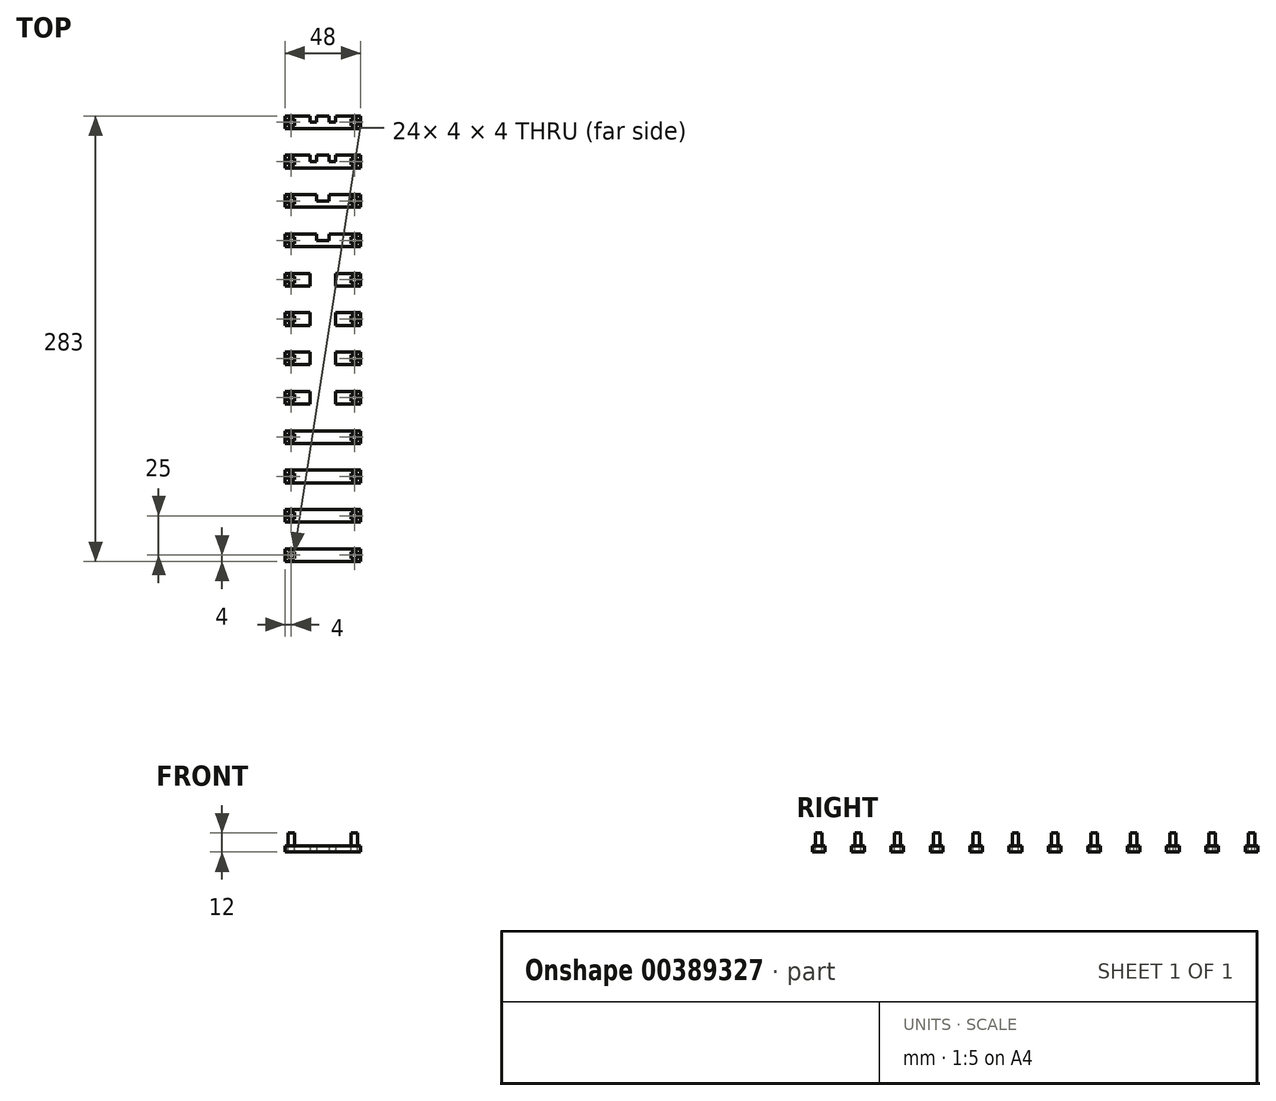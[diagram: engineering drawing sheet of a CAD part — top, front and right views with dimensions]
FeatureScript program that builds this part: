
annotation { "Feature Type Name" : "Feature", "Feature Type Description" : "" }
export const myFeature = defineFeature(function(context is Context, id is Id, definition is map)
    precondition{}
    {
        {
            assignVariable(context, id + "F0", {"name" : "WT", "anyValue" : 4});
        }
        {
            var Q0;
            Q0=qCreatedBy(makeId("Top.planeOp"),FACE);
            var sketch = newSketch(context, id + "F1", { "sketchPlane" : qUnion([Q0])});
            skLineSegment(sketch, "E0.bottom", {"start": v(-24, 4) * mm, "end": v(24, 4) * mm});
            skLineSegment(sketch, "E0.top", {"start": v(-24, -4) * mm, "end": v(24, -4) * mm});
            skLineSegment(sketch, "E0.left", {"start": v(-24, 4) * mm, "end": v(-24, -4) * mm});
            skLineSegment(sketch, "E0.right", {"start": v(24, 4) * mm, "end": v(24, -4) * mm});
            skPoint(sketch, "E0.middle", {"position": v(0, 0) * mm});
            skLineSegment(sketch, "E1.0.1.0", {"start": v(-24, 21) * mm, "end": v(24, 21) * mm});
            skLineSegment(sketch, "E1.0.1.1", {"start": v(-24, 29) * mm, "end": v(-24, 21) * mm});
            skLineSegment(sketch, "E1.0.1.2", {"start": v(-24, 29) * mm, "end": v(24, 29) * mm});
            skLineSegment(sketch, "E1.0.1.3", {"start": v(24, 29) * mm, "end": v(24, 21) * mm});
            skLineSegment(sketch, "E1.0.2.0", {"start": v(-24, 46) * mm, "end": v(24, 46) * mm});
            skLineSegment(sketch, "E1.0.2.1", {"start": v(-24, 54) * mm, "end": v(-24, 46) * mm});
            skLineSegment(sketch, "E1.0.2.2", {"start": v(-24, 54) * mm, "end": v(24, 54) * mm});
            skLineSegment(sketch, "E1.0.2.3", {"start": v(24, 54) * mm, "end": v(24, 46) * mm});
            skLineSegment(sketch, "E1.0.3.0", {"start": v(-24, 71) * mm, "end": v(24, 71) * mm});
            skLineSegment(sketch, "E1.0.3.1", {"start": v(-24, 79) * mm, "end": v(-24, 71) * mm});
            skLineSegment(sketch, "E1.0.3.2", {"start": v(-24, 79) * mm, "end": v(24, 79) * mm});
            skLineSegment(sketch, "E1.0.3.3", {"start": v(24, 79) * mm, "end": v(24, 71) * mm});
            skLineSegment(sketch, "E1.direction1", {"start": v(-35, -4) * mm, "end": v(-24, -4) * mm, "construction": true});
            skLineSegment(sketch, "E1.direction2", {"start": v(-24, -4) * mm, "end": v(-24, 21) * mm, "construction": true});
            skLineSegment(sketch, "E2.0.0.4", {"start": v(-24, 96) * mm, "end": v(24, 96) * mm});
            skLineSegment(sketch, "E2.3.0.4", {"start": v(-24, 104) * mm, "end": v(-24, 96) * mm});
            skLineSegment(sketch, "E2.6.0.4", {"start": v(-24, 104) * mm, "end": v(24, 104) * mm});
            skLineSegment(sketch, "E2.9.0.4", {"start": v(24, 104) * mm, "end": v(24, 96) * mm});
            skLineSegment(sketch, "E2.0.0.5", {"start": v(-24, 121) * mm, "end": v(24, 121) * mm});
            skLineSegment(sketch, "E2.3.0.5", {"start": v(-24, 129) * mm, "end": v(-24, 121) * mm});
            skLineSegment(sketch, "E2.6.0.5", {"start": v(-24, 129) * mm, "end": v(24, 129) * mm});
            skLineSegment(sketch, "E2.9.0.5", {"start": v(24, 129) * mm, "end": v(24, 121) * mm});
            skLineSegment(sketch, "E2.0.0.6", {"start": v(-24, 146) * mm, "end": v(24, 146) * mm});
            skLineSegment(sketch, "E2.3.0.6", {"start": v(-24, 154) * mm, "end": v(-24, 146) * mm});
            skLineSegment(sketch, "E2.6.0.6", {"start": v(-24, 154) * mm, "end": v(24, 154) * mm});
            skLineSegment(sketch, "E2.9.0.6", {"start": v(24, 154) * mm, "end": v(24, 146) * mm});
            skLineSegment(sketch, "E2.0.0.7", {"start": v(-24, 171) * mm, "end": v(24, 171) * mm});
            skLineSegment(sketch, "E2.3.0.7", {"start": v(-24, 179) * mm, "end": v(-24, 171) * mm});
            skLineSegment(sketch, "E2.6.0.7", {"start": v(-24, 179) * mm, "end": v(24, 179) * mm});
            skLineSegment(sketch, "E2.9.0.7", {"start": v(24, 179) * mm, "end": v(24, 171) * mm});
            skLineSegment(sketch, "E3", {"start": v(-8, 96) * mm, "end": v(-8, 179) * mm});
            skLineSegment(sketch, "E4", {"start": v(8, 179) * mm, "end": v(8, 96) * mm});
            skLineSegment(sketch, "E5.0.0.8", {"start": v(-24, 196) * mm, "end": v(24, 196) * mm});
            skLineSegment(sketch, "E5.3.0.8", {"start": v(-24, 204) * mm, "end": v(-24, 196) * mm});
            skLineSegment(sketch, "E5.6.0.8", {"start": v(-24, 204) * mm, "end": v(24, 204) * mm});
            skLineSegment(sketch, "E5.9.0.8", {"start": v(24, 204) * mm, "end": v(24, 196) * mm});
            skLineSegment(sketch, "E5.0.0.9", {"start": v(-24, 221) * mm, "end": v(24, 221) * mm});
            skLineSegment(sketch, "E5.3.0.9", {"start": v(-24, 229) * mm, "end": v(-24, 221) * mm});
            skLineSegment(sketch, "E5.6.0.9", {"start": v(-24, 229) * mm, "end": v(24, 229) * mm});
            skLineSegment(sketch, "E5.9.0.9", {"start": v(24, 229) * mm, "end": v(24, 221) * mm});
            skLineSegment(sketch, "E5.0.0.10", {"start": v(-24, 246) * mm, "end": v(24, 246) * mm});
            skLineSegment(sketch, "E5.3.0.10", {"start": v(-24, 254) * mm, "end": v(-24, 246) * mm});
            skLineSegment(sketch, "E5.6.0.10", {"start": v(-24, 254) * mm, "end": v(24, 254) * mm});
            skLineSegment(sketch, "E5.9.0.10", {"start": v(24, 254) * mm, "end": v(24, 246) * mm});
            skLineSegment(sketch, "E5.0.0.11", {"start": v(-24, 271) * mm, "end": v(24, 271) * mm});
            skLineSegment(sketch, "E5.3.0.11", {"start": v(-24, 279) * mm, "end": v(-24, 271) * mm});
            skLineSegment(sketch, "E5.6.0.11", {"start": v(-24, 279) * mm, "end": v(24, 279) * mm});
            skLineSegment(sketch, "E5.9.0.11", {"start": v(24, 279) * mm, "end": v(24, 271) * mm});
            skLineSegment(sketch, "E6", {"start": v(-4, 204) * mm, "end": v(-4, 200) * mm});
            skPoint(sketch, "E6.endSnap0", {"position": v(-24, 200) * mm});
            skLineSegment(sketch, "E7", {"start": v(-4, 200) * mm, "end": v(4, 200) * mm});
            skLineSegment(sketch, "E8", {"start": v(4, 200) * mm, "end": v(4, 204) * mm});
            skLineSegment(sketch, "E9", {"start": v(-4, 229) * mm, "end": v(-4, 225) * mm});
            skLineSegment(sketch, "E10", {"start": v(-4, 225) * mm, "end": v(4, 225) * mm});
            skLineSegment(sketch, "E11", {"start": v(4, 225) * mm, "end": v(4, 229) * mm});
            skLineSegment(sketch, "E12", {"start": v(-8, 254) * mm, "end": v(-8, 250) * mm});
            skLineSegment(sketch, "E13", {"start": v(-8, 250) * mm, "end": v(-4, 250) * mm});
            skLineSegment(sketch, "E14", {"start": v(-4, 250) * mm, "end": v(-4, 254) * mm});
            skLineSegment(sketch, "E15", {"start": v(8, 254) * mm, "end": v(8, 250) * mm});
            skLineSegment(sketch, "E16", {"start": v(4, 250) * mm, "end": v(8, 250) * mm});
            skLineSegment(sketch, "E17", {"start": v(4, 250) * mm, "end": v(4, 254) * mm});
            skLineSegment(sketch, "E18", {"start": v(-8, 275) * mm, "end": v(-8, 279) * mm});
            skLineSegment(sketch, "E19", {"start": v(-4, 275) * mm, "end": v(-4, 279) * mm});
            skLineSegment(sketch, "E20", {"start": v(4, 275) * mm, "end": v(4, 279) * mm});
            skLineSegment(sketch, "E21", {"start": v(8, 275) * mm, "end": v(8, 279) * mm});
            skLineSegment(sketch, "E22", {"start": v(-8, 275) * mm, "end": v(-4, 275) * mm});
            skLineSegment(sketch, "E23", {"start": v(4, 275) * mm, "end": v(8, 275) * mm});
            skLineSegment(sketch, "E24", {"start": v(0, 254) * mm, "end": v(0, 271) * mm, "construction": true});
            skLineSegment(sketch, "E25", {"start": v(0, 262.5) * mm, "end": v(-4.81, 262.5) * mm, "construction": true});
            skLineSegment(sketch, "E26", {"start": v(0, 246) * mm, "end": v(0, 229) * mm, "construction": true});
            skLineSegment(sketch, "E27", {"start": v(0, 221) * mm, "end": v(0, 204) * mm, "construction": true});
            skLineSegment(sketch, "E28", {"start": v(0, 237.5) * mm, "end": v(-7.24, 237.5) * mm, "construction": true});
            skLineSegment(sketch, "E29", {"start": v(0, 212.5) * mm, "end": v(-6.88, 212.5) * mm, "construction": true});
            skLineSegment(sketch, "E30", {"start": v(0, 196) * mm, "end": v(0, 179) * mm, "construction": true});
            skLineSegment(sketch, "E31", {"start": v(0, 187.5) * mm, "end": v(4.56, 187.5) * mm, "construction": true});
            skPoint(sketch, "E31.endSnap0", {"position": v(0, 187.5) * mm});
            skLineSegment(sketch, "E32", {"start": v(0, 171) * mm, "end": v(0, 154) * mm, "construction": true});
            skLineSegment(sketch, "E33", {"start": v(0, 162.5) * mm, "end": v(4.36, 162.5) * mm, "construction": true});
            skLineSegment(sketch, "E34", {"start": v(0, 146) * mm, "end": v(0, 129) * mm, "construction": true});
            skLineSegment(sketch, "E35", {"start": v(0, 137.5) * mm, "end": v(2.22, 137.5) * mm, "construction": true});
            skLineSegment(sketch, "E36", {"start": v(0, 121) * mm, "end": v(0, 104) * mm, "construction": true});
            skLineSegment(sketch, "E37", {"start": v(0, 112.5) * mm, "end": v(3.52, 112.5) * mm, "construction": true});
            skLineSegment(sketch, "E38", {"start": v(0, 96) * mm, "end": v(0, 79) * mm, "construction": true});
            skLineSegment(sketch, "E39", {"start": v(0, 87.5) * mm, "end": v(3.87, 87.5) * mm, "construction": true});
            skLineSegment(sketch, "E40", {"start": v(0, 71) * mm, "end": v(0, 54) * mm, "construction": true});
            skLineSegment(sketch, "E41", {"start": v(0, 62.5) * mm, "end": v(4.14, 62.5) * mm, "construction": true});
            skLineSegment(sketch, "E42", {"start": v(0, 46) * mm, "end": v(0, 29) * mm, "construction": true});
            skLineSegment(sketch, "E43", {"start": v(0, 37.5) * mm, "end": v(2.67, 37.5) * mm, "construction": true});
            skLineSegment(sketch, "E44", {"start": v(0, 21) * mm, "end": v(0, 4) * mm, "construction": true});
            skLineSegment(sketch, "E45", {"start": v(0, 12.5) * mm, "end": v(4.27, 12.5) * mm, "construction": true});
            skSolve(sketch);
        }
        {
            var Q0;
            Q0=makeQuery(id+"F1.imprint","IMPRINT",FACE,{"disambiguationData":[TD([[makeQuery(id+"F1.imprint","IMPRINT",EDGE,{"derivedFrom":sQuery(id+"F1.wireOp",EDGE,"E0.bottom")}),-1.0]])]});
            var Q1;
            Q1=makeQuery(id+"F1.imprint","IMPRINT",FACE,{"disambiguationData":[TD([[makeQuery(id+"F1.imprint","IMPRINT",EDGE,{"derivedFrom":sQuery(id+"F1.wireOp",EDGE,"E1.0.1.0")}),1.0]])]});
            var Q2;
            Q2=makeQuery(id+"F1.imprint","IMPRINT",FACE,{"disambiguationData":[TD([[makeQuery(id+"F1.imprint","IMPRINT",EDGE,{"derivedFrom":sQuery(id+"F1.wireOp",EDGE,"E1.0.2.0")}),1.0]])]});
            var Q3;
            Q3=makeQuery(id+"F1.imprint","IMPRINT",FACE,{"disambiguationData":[TD([[makeQuery(id+"F1.imprint","IMPRINT",EDGE,{"derivedFrom":sQuery(id+"F1.wireOp",EDGE,"E1.0.3.0")}),1.0]])]});
            var Q4;
            Q4=makeQuery(id+"F1.imprint","IMPRINT",FACE,{"disambiguationData":[TD([[makeQuery(id+"F1.imprint","IMPRINT",EDGE,{"derivedFrom":sQuery(id+"F1.wireOp",EDGE,"E1.0.4.0")}),1.0]])]});
            var Q5;
            {var subQ0=sQuery(id+"F1.wireOp",EDGE,"E2.3.0.4");Q5=makeQuery(id+"F1.imprint","IMPRINT",FACE,{"disambiguationData":[TD([[makeQuery(id+"F1.imprint","IMPRINT",EDGE,{"derivedFrom":subQ0}),1.0]])]});}
            var Q6;
            {var subQ0=sQuery(id+"F1.wireOp",EDGE,"E2.3.0.5");Q6=makeQuery(id+"F1.imprint","IMPRINT",FACE,{"disambiguationData":[TD([[makeQuery(id+"F1.imprint","IMPRINT",EDGE,{"derivedFrom":subQ0}),1.0]])]});}
            var Q7;
            {var subQ0=sQuery(id+"F1.wireOp",EDGE,"E2.3.0.6");Q7=makeQuery(id+"F1.imprint","IMPRINT",FACE,{"disambiguationData":[TD([[makeQuery(id+"F1.imprint","IMPRINT",EDGE,{"derivedFrom":subQ0}),1.0]])]});}
            var Q8;
            {var subQ0=sQuery(id+"F1.wireOp",EDGE,"E2.3.0.7");Q8=makeQuery(id+"F1.imprint","IMPRINT",FACE,{"disambiguationData":[TD([[makeQuery(id+"F1.imprint","IMPRINT",EDGE,{"derivedFrom":subQ0}),1.0]])]});}
            var Q9;
            {var subQ0=sQuery(id+"F1.wireOp",EDGE,"E2.9.0.7");Q9=makeQuery(id+"F1.imprint","IMPRINT",FACE,{"disambiguationData":[TD([[makeQuery(id+"F1.imprint","IMPRINT",EDGE,{"derivedFrom":subQ0}),-1.0]])]});}
            var Q10;
            {var subQ0=sQuery(id+"F1.wireOp",EDGE,"E2.9.0.6");Q10=makeQuery(id+"F1.imprint","IMPRINT",FACE,{"disambiguationData":[TD([[makeQuery(id+"F1.imprint","IMPRINT",EDGE,{"derivedFrom":subQ0}),-1.0]])]});}
            var Q11;
            {var subQ0=sQuery(id+"F1.wireOp",EDGE,"E2.9.0.5");Q11=makeQuery(id+"F1.imprint","IMPRINT",FACE,{"disambiguationData":[TD([[makeQuery(id+"F1.imprint","IMPRINT",EDGE,{"derivedFrom":subQ0}),-1.0]])]});}
            var Q12;
            {var subQ0=sQuery(id+"F1.wireOp",EDGE,"E2.9.0.4");Q12=makeQuery(id+"F1.imprint","IMPRINT",FACE,{"disambiguationData":[TD([[makeQuery(id+"F1.imprint","IMPRINT",EDGE,{"derivedFrom":subQ0}),-1.0]])]});}
            var Q13;
            Q13=makeQuery(id+"F1.imprint","IMPRINT",FACE,{"disambiguationData":[TD([[makeQuery(id+"F1.imprint","IMPRINT",EDGE,{"derivedFrom":sQuery(id+"F1.wireOp",EDGE,"E5.0.0.8")}),1.0]])]});
            var Q14;
            Q14=makeQuery(id+"F1.imprint","IMPRINT",FACE,{"disambiguationData":[TD([[makeQuery(id+"F1.imprint","IMPRINT",EDGE,{"derivedFrom":sQuery(id+"F1.wireOp",EDGE,"E5.0.0.9")}),1.0]])]});
            var Q15;
            Q15=makeQuery(id+"F1.imprint","IMPRINT",FACE,{"disambiguationData":[TD([[makeQuery(id+"F1.imprint","IMPRINT",EDGE,{"derivedFrom":sQuery(id+"F1.wireOp",EDGE,"E5.0.0.10")}),1.0]])]});
            var Q16;
            Q16=makeQuery(id+"F1.imprint","IMPRINT",FACE,{"disambiguationData":[TD([[makeQuery(id+"F1.imprint","IMPRINT",EDGE,{"derivedFrom":sQuery(id+"F1.wireOp",EDGE,"E5.0.0.11")}),1.0]])]});
            extrude(context, id + "F2", {"entities" : qUnion([Q0, Q1, Q2, Q3, Q4, Q5, Q6, Q7, Q8, Q9, Q10, Q11, Q12, Q13, Q14, Q15, Q16]), "depth" : getVariable(context, 'WT') * mm});
        }
        {
            var Q0;
            Q0=makeQuery(id+"F2.opExtrude","CAP_FACE",FACE,{"disambiguationData":[OSD([sQuery(id+"F1.wireOp",EDGE,"E5.0.0.11"),sQuery(id+"F1.wireOp",EDGE,"E5.3.0.11"),sQuery(id+"F1.wireOp",EDGE,"E5.6.0.11"),sQuery(id+"F1.wireOp",EDGE,"E5.9.0.11"),sQuery(id+"F1.wireOp",EDGE,"E18"),sQuery(id+"F1.wireOp",EDGE,"E19"),sQuery(id+"F1.wireOp",EDGE,"E20"),sQuery(id+"F1.wireOp",EDGE,"E21"),sQuery(id+"F1.wireOp",EDGE,"E22"),sQuery(id+"F1.wireOp",EDGE,"E23")])],"isStart":false});
            var sketch = newSketch(context, id + "F3", { "sketchPlane" : qUnion([Q0])});
            skLineSegment(sketch, "E46", {"start": v(0, 279) * mm, "end": v(0, 302.45) * mm, "construction": true});
            skLineSegment(sketch, "E47.bottom", {"start": v(-22, 277) * mm, "end": v(-18, 277) * mm});
            skLineSegment(sketch, "E47.top", {"start": v(-22, 273) * mm, "end": v(-18, 273) * mm});
            skLineSegment(sketch, "E47.left", {"start": v(-22, 277) * mm, "end": v(-22, 273) * mm});
            skLineSegment(sketch, "E47.right", {"start": v(-18, 277) * mm, "end": v(-18, 273) * mm});
            skPoint(sketch, "E47.middle", {"position": v(-20, 275) * mm});
            skPoint(sketch, "E48", {"position": v(-24, 275) * mm});
            skLineSegment(sketch, "E49.MirrorCS", {"start": v(18, 277) * mm, "end": v(18, 273) * mm});
            skLineSegment(sketch, "E50.MirrorCS", {"start": v(22, 277) * mm, "end": v(18, 277) * mm});
            skLineSegment(sketch, "E51.MirrorCS", {"start": v(22, 277) * mm, "end": v(22, 273) * mm});
            skLineSegment(sketch, "E52.MirrorCS", {"start": v(22, 273) * mm, "end": v(18, 273) * mm});
            skLineSegment(sketch, "E53.MirrorCS", {"start": v(-18, 248) * mm, "end": v(-18, 252) * mm});
            skLineSegment(sketch, "E54.MirrorCS", {"start": v(-22, 252) * mm, "end": v(-18, 252) * mm});
            skLineSegment(sketch, "E55.MirrorCS", {"start": v(-22, 248) * mm, "end": v(-18, 248) * mm});
            skLineSegment(sketch, "E56.MirrorCS", {"start": v(-22, 248) * mm, "end": v(-22, 252) * mm});
            skLineSegment(sketch, "E57.MirrorCS", {"start": v(18, 248) * mm, "end": v(18, 252) * mm});
            skLineSegment(sketch, "E58.MirrorCS", {"start": v(22, 248) * mm, "end": v(18, 248) * mm});
            skLineSegment(sketch, "E59.MirrorCS", {"start": v(22, 248) * mm, "end": v(22, 252) * mm});
            skLineSegment(sketch, "E60.MirrorCS", {"start": v(22, 252) * mm, "end": v(18, 252) * mm});
            skLineSegment(sketch, "E61.MirrorCS", {"start": v(-22, 227) * mm, "end": v(-18, 227) * mm});
            skLineSegment(sketch, "E62.MirrorCS", {"start": v(-18, 227) * mm, "end": v(-18, 223) * mm});
            skLineSegment(sketch, "E63.MirrorCS", {"start": v(-22, 223) * mm, "end": v(-18, 223) * mm});
            skLineSegment(sketch, "E64.MirrorCS", {"start": v(-22, 227) * mm, "end": v(-22, 223) * mm});
            skLineSegment(sketch, "E65.MirrorCS", {"start": v(18, 227) * mm, "end": v(18, 223) * mm});
            skLineSegment(sketch, "E66.MirrorCS", {"start": v(22, 223) * mm, "end": v(18, 223) * mm});
            skLineSegment(sketch, "E67.MirrorCS", {"start": v(22, 227) * mm, "end": v(22, 223) * mm});
            skLineSegment(sketch, "E68.MirrorCS", {"start": v(22, 227) * mm, "end": v(18, 227) * mm});
            skLineSegment(sketch, "E69.MirrorCS", {"start": v(-22, 202) * mm, "end": v(-18, 202) * mm});
            skLineSegment(sketch, "E70.MirrorCS", {"start": v(-18, 198) * mm, "end": v(-18, 202) * mm});
            skLineSegment(sketch, "E71.MirrorCS", {"start": v(-22, 198) * mm, "end": v(-18, 198) * mm});
            skLineSegment(sketch, "E72.MirrorCS", {"start": v(-22, 198) * mm, "end": v(-22, 202) * mm});
            skLineSegment(sketch, "E73.MirrorCS", {"start": v(22, 202) * mm, "end": v(18, 202) * mm});
            skLineSegment(sketch, "E74.MirrorCS", {"start": v(18, 198) * mm, "end": v(18, 202) * mm});
            skLineSegment(sketch, "E75.MirrorCS", {"start": v(22, 198) * mm, "end": v(18, 198) * mm});
            skLineSegment(sketch, "E76.MirrorCS", {"start": v(22, 198) * mm, "end": v(22, 202) * mm});
            skLineSegment(sketch, "E77.MirrorCS", {"start": v(-18, 177) * mm, "end": v(-18, 173) * mm});
            skLineSegment(sketch, "E78.MirrorCS", {"start": v(-22, 173) * mm, "end": v(-18, 173) * mm});
            skLineSegment(sketch, "E79.MirrorCS", {"start": v(-22, 177) * mm, "end": v(-22, 173) * mm});
            skLineSegment(sketch, "E80.MirrorCS", {"start": v(-22, 177) * mm, "end": v(-18, 177) * mm});
            skLineSegment(sketch, "E81.MirrorCS", {"start": v(18, 177) * mm, "end": v(18, 173) * mm});
            skLineSegment(sketch, "E82.MirrorCS", {"start": v(22, 173) * mm, "end": v(18, 173) * mm});
            skLineSegment(sketch, "E83.MirrorCS", {"start": v(22, 177) * mm, "end": v(22, 173) * mm});
            skLineSegment(sketch, "E84.MirrorCS", {"start": v(22, 177) * mm, "end": v(18, 177) * mm});
            skLineSegment(sketch, "E85.MirrorCS", {"start": v(-22, 152) * mm, "end": v(-18, 152) * mm});
            skLineSegment(sketch, "E86.MirrorCS", {"start": v(-22, 148) * mm, "end": v(-22, 152) * mm});
            skLineSegment(sketch, "E87.MirrorCS", {"start": v(-22, 148) * mm, "end": v(-18, 148) * mm});
            skLineSegment(sketch, "E88.MirrorCS", {"start": v(-18, 148) * mm, "end": v(-18, 152) * mm});
            skLineSegment(sketch, "E89.MirrorCS", {"start": v(22, 152) * mm, "end": v(18, 152) * mm});
            skLineSegment(sketch, "E90.MirrorCS", {"start": v(18, 148) * mm, "end": v(18, 152) * mm});
            skLineSegment(sketch, "E91.MirrorCS", {"start": v(22, 148) * mm, "end": v(18, 148) * mm});
            skLineSegment(sketch, "E92.MirrorCS", {"start": v(22, 148) * mm, "end": v(22, 152) * mm});
            skLineSegment(sketch, "E93.MirrorCS", {"start": v(-18, 127) * mm, "end": v(-18, 123) * mm});
            skLineSegment(sketch, "E94.MirrorCS", {"start": v(-22, 123) * mm, "end": v(-18, 123) * mm});
            skLineSegment(sketch, "E95.MirrorCS", {"start": v(-22, 127) * mm, "end": v(-22, 123) * mm});
            skLineSegment(sketch, "E96.MirrorCS", {"start": v(-22, 127) * mm, "end": v(-18, 127) * mm});
            skLineSegment(sketch, "E97.MirrorCS", {"start": v(22, 123) * mm, "end": v(18, 123) * mm});
            skLineSegment(sketch, "E98.MirrorCS", {"start": v(18, 127) * mm, "end": v(18, 123) * mm});
            skLineSegment(sketch, "E99.MirrorCS", {"start": v(22, 127) * mm, "end": v(22, 123) * mm});
            skLineSegment(sketch, "E100.MirrorCS", {"start": v(22, 127) * mm, "end": v(18, 127) * mm});
            skLineSegment(sketch, "E101.MirrorCS", {"start": v(-22, 102) * mm, "end": v(-18, 102) * mm});
            skLineSegment(sketch, "E102.MirrorCS", {"start": v(-18, 98) * mm, "end": v(-18, 102) * mm});
            skLineSegment(sketch, "E103.MirrorCS", {"start": v(-22, 98) * mm, "end": v(-18, 98) * mm});
            skLineSegment(sketch, "E104.MirrorCS", {"start": v(-22, 98) * mm, "end": v(-22, 102) * mm});
            skLineSegment(sketch, "E105.MirrorCS", {"start": v(22, 102) * mm, "end": v(18, 102) * mm});
            skLineSegment(sketch, "E106.MirrorCS", {"start": v(18, 98) * mm, "end": v(18, 102) * mm});
            skLineSegment(sketch, "E107.MirrorCS", {"start": v(22, 98) * mm, "end": v(18, 98) * mm});
            skLineSegment(sketch, "E108.MirrorCS", {"start": v(22, 98) * mm, "end": v(22, 102) * mm});
            skLineSegment(sketch, "E109.MirrorCS", {"start": v(-22, 77) * mm, "end": v(-22, 73) * mm});
            skLineSegment(sketch, "E110.MirrorCS", {"start": v(-22, 73) * mm, "end": v(-18, 73) * mm});
            skLineSegment(sketch, "E111.MirrorCS", {"start": v(-18, 77) * mm, "end": v(-18, 73) * mm});
            skLineSegment(sketch, "E112.MirrorCS", {"start": v(-22, 77) * mm, "end": v(-18, 77) * mm});
            skLineSegment(sketch, "E113.MirrorCS", {"start": v(18, 77) * mm, "end": v(18, 73) * mm});
            skLineSegment(sketch, "E114.MirrorCS", {"start": v(22, 73) * mm, "end": v(18, 73) * mm});
            skLineSegment(sketch, "E115.MirrorCS", {"start": v(22, 77) * mm, "end": v(22, 73) * mm});
            skLineSegment(sketch, "E116.MirrorCS", {"start": v(22, 77) * mm, "end": v(18, 77) * mm});
            skLineSegment(sketch, "E117.MirrorCS", {"start": v(18, 48) * mm, "end": v(18, 52) * mm});
            skLineSegment(sketch, "E118.MirrorCS", {"start": v(22, 48) * mm, "end": v(18, 48) * mm});
            skLineSegment(sketch, "E119.MirrorCS", {"start": v(22, 48) * mm, "end": v(22, 52) * mm});
            skLineSegment(sketch, "E120.MirrorCS", {"start": v(22, 52) * mm, "end": v(18, 52) * mm});
            skLineSegment(sketch, "E121.MirrorCS", {"start": v(-22, 48) * mm, "end": v(-22, 52) * mm});
            skLineSegment(sketch, "E122.MirrorCS", {"start": v(-22, 48) * mm, "end": v(-18, 48) * mm});
            skLineSegment(sketch, "E123.MirrorCS", {"start": v(-18, 48) * mm, "end": v(-18, 52) * mm});
            skLineSegment(sketch, "E124.MirrorCS", {"start": v(-22, 52) * mm, "end": v(-18, 52) * mm});
            skLineSegment(sketch, "E125.MirrorCS", {"start": v(-22, 27) * mm, "end": v(-22, 23) * mm});
            skLineSegment(sketch, "E126.MirrorCS", {"start": v(-22, 23) * mm, "end": v(-18, 23) * mm});
            skLineSegment(sketch, "E127.MirrorCS", {"start": v(-18, 27) * mm, "end": v(-18, 23) * mm});
            skLineSegment(sketch, "E128.MirrorCS", {"start": v(-22, 27) * mm, "end": v(-18, 27) * mm});
            skLineSegment(sketch, "E129.MirrorCS", {"start": v(18, 27) * mm, "end": v(18, 23) * mm});
            skLineSegment(sketch, "E130.MirrorCS", {"start": v(22, 23) * mm, "end": v(18, 23) * mm});
            skLineSegment(sketch, "E131.MirrorCS", {"start": v(22, 27) * mm, "end": v(22, 23) * mm});
            skLineSegment(sketch, "E132.MirrorCS", {"start": v(22, 27) * mm, "end": v(18, 27) * mm});
            skLineSegment(sketch, "E133.MirrorCS", {"start": v(-18, -2) * mm, "end": v(-18, 2) * mm});
            skLineSegment(sketch, "E134.MirrorCS", {"start": v(-22, -2) * mm, "end": v(-18, -2) * mm});
            skLineSegment(sketch, "E135.MirrorCS", {"start": v(-22, -2) * mm, "end": v(-22, 2) * mm});
            skLineSegment(sketch, "E136.MirrorCS", {"start": v(-22, 2) * mm, "end": v(-18, 2) * mm});
            skLineSegment(sketch, "E137.MirrorCS", {"start": v(22, 2) * mm, "end": v(18, 2) * mm});
            skLineSegment(sketch, "E138.MirrorCS", {"start": v(18, -2) * mm, "end": v(18, 2) * mm});
            skLineSegment(sketch, "E139.MirrorCS", {"start": v(22, -2) * mm, "end": v(18, -2) * mm});
            skLineSegment(sketch, "E140.MirrorCS", {"start": v(22, -2) * mm, "end": v(22, 2) * mm});
            skSolve(sketch);
        }
        {
            var Q0;
            Q0=makeQuery(id+"F3.imprint","IMPRINT",FACE,{"disambiguationData":[TD([[makeQuery(id+"F3.imprint","IMPRINT",EDGE,{"derivedFrom":sQuery(id+"F3.wireOp",EDGE,"E49.MirrorCS")}),1.0]])]});
            var Q1;
            Q1=makeQuery(id+"F3.imprint","IMPRINT",FACE,{"disambiguationData":[TD([[makeQuery(id+"F3.imprint","IMPRINT",EDGE,{"derivedFrom":sQuery(id+"F3.wireOp",EDGE,"E47.bottom")}),-1.0]])]});
            var Q2;
            Q2=makeQuery(id+"F3.imprint","IMPRINT",FACE,{"disambiguationData":[TD([[makeQuery(id+"F3.imprint","IMPRINT",EDGE,{"derivedFrom":sQuery(id+"F3.wireOp",EDGE,"E53.MirrorCS")}),1.0]])]});
            var Q3;
            Q3=makeQuery(id+"F3.imprint","IMPRINT",FACE,{"disambiguationData":[TD([[makeQuery(id+"F3.imprint","IMPRINT",EDGE,{"derivedFrom":sQuery(id+"F3.wireOp",EDGE,"E58.MirrorCS")}),-1.0]])]});
            var Q4;
            Q4=makeQuery(id+"F3.imprint","IMPRINT",FACE,{"disambiguationData":[TD([[makeQuery(id+"F3.imprint","IMPRINT",EDGE,{"derivedFrom":sQuery(id+"F3.wireOp",EDGE,"E61.MirrorCS")}),-1.0]])]});
            var Q5;
            Q5=makeQuery(id+"F3.imprint","IMPRINT",FACE,{"disambiguationData":[TD([[makeQuery(id+"F3.imprint","IMPRINT",EDGE,{"derivedFrom":sQuery(id+"F3.wireOp",EDGE,"E65.MirrorCS")}),1.0]])]});
            var Q6;
            Q6=makeQuery(id+"F3.imprint","IMPRINT",FACE,{"disambiguationData":[TD([[makeQuery(id+"F3.imprint","IMPRINT",EDGE,{"derivedFrom":sQuery(id+"F3.wireOp",EDGE,"E69.MirrorCS")}),-1.0]])]});
            var Q7;
            Q7=makeQuery(id+"F3.imprint","IMPRINT",FACE,{"disambiguationData":[TD([[makeQuery(id+"F3.imprint","IMPRINT",EDGE,{"derivedFrom":sQuery(id+"F3.wireOp",EDGE,"E73.MirrorCS")}),1.0]])]});
            var Q8;
            Q8=makeQuery(id+"F3.imprint","IMPRINT",FACE,{"disambiguationData":[TD([[makeQuery(id+"F3.imprint","IMPRINT",EDGE,{"derivedFrom":sQuery(id+"F3.wireOp",EDGE,"E77.MirrorCS")}),-1.0]])]});
            var Q9;
            Q9=makeQuery(id+"F3.imprint","IMPRINT",FACE,{"disambiguationData":[TD([[makeQuery(id+"F3.imprint","IMPRINT",EDGE,{"derivedFrom":sQuery(id+"F3.wireOp",EDGE,"E81.MirrorCS")}),1.0]])]});
            var Q10;
            Q10=makeQuery(id+"F3.imprint","IMPRINT",FACE,{"disambiguationData":[TD([[makeQuery(id+"F3.imprint","IMPRINT",EDGE,{"derivedFrom":sQuery(id+"F3.wireOp",EDGE,"E86.MirrorCS")}),-1.0]])]});
            var Q11;
            Q11=makeQuery(id+"F3.imprint","IMPRINT",FACE,{"disambiguationData":[TD([[makeQuery(id+"F3.imprint","IMPRINT",EDGE,{"derivedFrom":sQuery(id+"F3.wireOp",EDGE,"E89.MirrorCS")}),1.0]])]});
            var Q12;
            Q12=makeQuery(id+"F3.imprint","IMPRINT",FACE,{"disambiguationData":[TD([[makeQuery(id+"F3.imprint","IMPRINT",EDGE,{"derivedFrom":sQuery(id+"F3.wireOp",EDGE,"E93.MirrorCS")}),-1.0]])]});
            var Q13;
            Q13=makeQuery(id+"F3.imprint","IMPRINT",FACE,{"disambiguationData":[TD([[makeQuery(id+"F3.imprint","IMPRINT",EDGE,{"derivedFrom":sQuery(id+"F3.wireOp",EDGE,"E97.MirrorCS")}),-1.0]])]});
            var Q14;
            Q14=makeQuery(id+"F3.imprint","IMPRINT",FACE,{"disambiguationData":[TD([[makeQuery(id+"F3.imprint","IMPRINT",EDGE,{"derivedFrom":sQuery(id+"F3.wireOp",EDGE,"E101.MirrorCS")}),-1.0]])]});
            var Q15;
            Q15=makeQuery(id+"F3.imprint","IMPRINT",FACE,{"disambiguationData":[TD([[makeQuery(id+"F3.imprint","IMPRINT",EDGE,{"derivedFrom":sQuery(id+"F3.wireOp",EDGE,"E105.MirrorCS")}),1.0]])]});
            var Q16;
            Q16=makeQuery(id+"F3.imprint","IMPRINT",FACE,{"disambiguationData":[TD([[makeQuery(id+"F3.imprint","IMPRINT",EDGE,{"derivedFrom":sQuery(id+"F3.wireOp",EDGE,"E109.MirrorCS")}),1.0]])]});
            var Q17;
            Q17=makeQuery(id+"F3.imprint","IMPRINT",FACE,{"disambiguationData":[TD([[makeQuery(id+"F3.imprint","IMPRINT",EDGE,{"derivedFrom":sQuery(id+"F3.wireOp",EDGE,"E113.MirrorCS")}),1.0]])]});
            var Q18;
            Q18=makeQuery(id+"F3.imprint","IMPRINT",FACE,{"disambiguationData":[TD([[makeQuery(id+"F3.imprint","IMPRINT",EDGE,{"derivedFrom":sQuery(id+"F3.wireOp",EDGE,"E117.MirrorCS")}),-1.0]])]});
            var Q19;
            Q19=makeQuery(id+"F3.imprint","IMPRINT",FACE,{"disambiguationData":[TD([[makeQuery(id+"F3.imprint","IMPRINT",EDGE,{"derivedFrom":sQuery(id+"F3.wireOp",EDGE,"E121.MirrorCS")}),-1.0]])]});
            var Q20;
            Q20=makeQuery(id+"F3.imprint","IMPRINT",FACE,{"disambiguationData":[TD([[makeQuery(id+"F3.imprint","IMPRINT",EDGE,{"derivedFrom":sQuery(id+"F3.wireOp",EDGE,"E125.MirrorCS")}),1.0]])]});
            var Q21;
            Q21=makeQuery(id+"F3.imprint","IMPRINT",FACE,{"disambiguationData":[TD([[makeQuery(id+"F3.imprint","IMPRINT",EDGE,{"derivedFrom":sQuery(id+"F3.wireOp",EDGE,"E129.MirrorCS")}),1.0]])]});
            var Q22;
            Q22=makeQuery(id+"F3.imprint","IMPRINT",FACE,{"disambiguationData":[TD([[makeQuery(id+"F3.imprint","IMPRINT",EDGE,{"derivedFrom":sQuery(id+"F3.wireOp",EDGE,"E133.MirrorCS")}),1.0]])]});
            var Q23;
            Q23=makeQuery(id+"F3.imprint","IMPRINT",FACE,{"disambiguationData":[TD([[makeQuery(id+"F3.imprint","IMPRINT",EDGE,{"derivedFrom":sQuery(id+"F3.wireOp",EDGE,"E137.MirrorCS")}),1.0]])]});
            extrude(context, id + "F4", {"entities" : qUnion([Q0, Q1, Q2, Q3, Q4, Q5, Q6, Q7, Q8, Q9, Q10, Q11, Q12, Q13, Q14, Q15, Q16, Q17, Q18, Q19, Q20, Q21, Q22, Q23]), "operationType" : NewBodyOperationType.REMOVE, "endBound" : BoundingType.THROUGH_ALL, "oppositeDirection" : true, "depth" : 25 * mm});
        }
        {
            var Q0;
            Q0=makeQuery(id+"F3.imprint","IMPRINT",FACE,{"disambiguationData":[TD([[makeQuery(id+"F3.imprint","IMPRINT",EDGE,{"derivedFrom":sQuery(id+"F3.wireOp",EDGE,"E133.MirrorCS")}),1.0]])]});
            var Q1;
            Q1=makeQuery(id+"F3.imprint","IMPRINT",FACE,{"disambiguationData":[TD([[makeQuery(id+"F3.imprint","IMPRINT",EDGE,{"derivedFrom":sQuery(id+"F3.wireOp",EDGE,"E137.MirrorCS")}),1.0]])]});
            var Q2;
            Q2=makeQuery(id+"F3.imprint","IMPRINT",FACE,{"disambiguationData":[TD([[makeQuery(id+"F3.imprint","IMPRINT",EDGE,{"derivedFrom":sQuery(id+"F3.wireOp",EDGE,"E129.MirrorCS")}),1.0]])]});
            var Q3;
            Q3=makeQuery(id+"F3.imprint","IMPRINT",FACE,{"disambiguationData":[TD([[makeQuery(id+"F3.imprint","IMPRINT",EDGE,{"derivedFrom":sQuery(id+"F3.wireOp",EDGE,"E125.MirrorCS")}),1.0]])]});
            var Q4;
            Q4=makeQuery(id+"F3.imprint","IMPRINT",FACE,{"disambiguationData":[TD([[makeQuery(id+"F3.imprint","IMPRINT",EDGE,{"derivedFrom":sQuery(id+"F3.wireOp",EDGE,"E121.MirrorCS")}),-1.0]])]});
            var Q5;
            Q5=makeQuery(id+"F3.imprint","IMPRINT",FACE,{"disambiguationData":[TD([[makeQuery(id+"F3.imprint","IMPRINT",EDGE,{"derivedFrom":sQuery(id+"F3.wireOp",EDGE,"E109.MirrorCS")}),1.0]])]});
            var Q6;
            Q6=makeQuery(id+"F3.imprint","IMPRINT",FACE,{"disambiguationData":[TD([[makeQuery(id+"F3.imprint","IMPRINT",EDGE,{"derivedFrom":sQuery(id+"F3.wireOp",EDGE,"E113.MirrorCS")}),1.0]])]});
            var Q7;
            Q7=makeQuery(id+"F3.imprint","IMPRINT",FACE,{"disambiguationData":[TD([[makeQuery(id+"F3.imprint","IMPRINT",EDGE,{"derivedFrom":sQuery(id+"F3.wireOp",EDGE,"E117.MirrorCS")}),-1.0]])]});
            var Q8;
            Q8=makeQuery(id+"F3.imprint","IMPRINT",FACE,{"disambiguationData":[TD([[makeQuery(id+"F3.imprint","IMPRINT",EDGE,{"derivedFrom":sQuery(id+"F3.wireOp",EDGE,"E105.MirrorCS")}),1.0]])]});
            var Q9;
            Q9=makeQuery(id+"F3.imprint","IMPRINT",FACE,{"disambiguationData":[TD([[makeQuery(id+"F3.imprint","IMPRINT",EDGE,{"derivedFrom":sQuery(id+"F3.wireOp",EDGE,"E101.MirrorCS")}),-1.0]])]});
            var Q10;
            Q10=makeQuery(id+"F3.imprint","IMPRINT",FACE,{"disambiguationData":[TD([[makeQuery(id+"F3.imprint","IMPRINT",EDGE,{"derivedFrom":sQuery(id+"F3.wireOp",EDGE,"E93.MirrorCS")}),-1.0]])]});
            var Q11;
            Q11=makeQuery(id+"F3.imprint","IMPRINT",FACE,{"disambiguationData":[TD([[makeQuery(id+"F3.imprint","IMPRINT",EDGE,{"derivedFrom":sQuery(id+"F3.wireOp",EDGE,"E97.MirrorCS")}),-1.0]])]});
            var Q12;
            Q12=makeQuery(id+"F3.imprint","IMPRINT",FACE,{"disambiguationData":[TD([[makeQuery(id+"F3.imprint","IMPRINT",EDGE,{"derivedFrom":sQuery(id+"F3.wireOp",EDGE,"E89.MirrorCS")}),1.0]])]});
            var Q13;
            Q13=makeQuery(id+"F3.imprint","IMPRINT",FACE,{"disambiguationData":[TD([[makeQuery(id+"F3.imprint","IMPRINT",EDGE,{"derivedFrom":sQuery(id+"F3.wireOp",EDGE,"E86.MirrorCS")}),-1.0]])]});
            var Q14;
            Q14=makeQuery(id+"F3.imprint","IMPRINT",FACE,{"disambiguationData":[TD([[makeQuery(id+"F3.imprint","IMPRINT",EDGE,{"derivedFrom":sQuery(id+"F3.wireOp",EDGE,"E77.MirrorCS")}),-1.0]])]});
            var Q15;
            Q15=makeQuery(id+"F3.imprint","IMPRINT",FACE,{"disambiguationData":[TD([[makeQuery(id+"F3.imprint","IMPRINT",EDGE,{"derivedFrom":sQuery(id+"F3.wireOp",EDGE,"E81.MirrorCS")}),1.0]])]});
            var Q16;
            Q16=makeQuery(id+"F3.imprint","IMPRINT",FACE,{"disambiguationData":[TD([[makeQuery(id+"F3.imprint","IMPRINT",EDGE,{"derivedFrom":sQuery(id+"F3.wireOp",EDGE,"E69.MirrorCS")}),-1.0]])]});
            var Q17;
            Q17=makeQuery(id+"F3.imprint","IMPRINT",FACE,{"disambiguationData":[TD([[makeQuery(id+"F3.imprint","IMPRINT",EDGE,{"derivedFrom":sQuery(id+"F3.wireOp",EDGE,"E73.MirrorCS")}),1.0]])]});
            var Q18;
            Q18=makeQuery(id+"F3.imprint","IMPRINT",FACE,{"disambiguationData":[TD([[makeQuery(id+"F3.imprint","IMPRINT",EDGE,{"derivedFrom":sQuery(id+"F3.wireOp",EDGE,"E65.MirrorCS")}),1.0]])]});
            var Q19;
            Q19=makeQuery(id+"F3.imprint","IMPRINT",FACE,{"disambiguationData":[TD([[makeQuery(id+"F3.imprint","IMPRINT",EDGE,{"derivedFrom":sQuery(id+"F3.wireOp",EDGE,"E61.MirrorCS")}),-1.0]])]});
            var Q20;
            Q20=makeQuery(id+"F3.imprint","IMPRINT",FACE,{"disambiguationData":[TD([[makeQuery(id+"F3.imprint","IMPRINT",EDGE,{"derivedFrom":sQuery(id+"F3.wireOp",EDGE,"E53.MirrorCS")}),1.0]])]});
            var Q21;
            Q21=makeQuery(id+"F3.imprint","IMPRINT",FACE,{"disambiguationData":[TD([[makeQuery(id+"F3.imprint","IMPRINT",EDGE,{"derivedFrom":sQuery(id+"F3.wireOp",EDGE,"E58.MirrorCS")}),-1.0]])]});
            var Q22;
            Q22=makeQuery(id+"F3.imprint","IMPRINT",FACE,{"disambiguationData":[TD([[makeQuery(id+"F3.imprint","IMPRINT",EDGE,{"derivedFrom":sQuery(id+"F3.wireOp",EDGE,"E49.MirrorCS")}),1.0]])]});
            var Q23;
            Q23=makeQuery(id+"F3.imprint","IMPRINT",FACE,{"disambiguationData":[TD([[makeQuery(id+"F3.imprint","IMPRINT",EDGE,{"derivedFrom":sQuery(id+"F3.wireOp",EDGE,"E47.bottom")}),-1.0]])]});
            extrude(context, id + "F5", {"entities" : qUnion([Q0, Q1, Q2, Q3, Q4, Q5, Q6, Q7, Q8, Q9, Q10, Q11, Q12, Q13, Q14, Q15, Q16, Q17, Q18, Q19, Q20, Q21, Q22, Q23]), "depth" : (getVariable(context, 'WT')) * 2 * mm});
        }
    });
